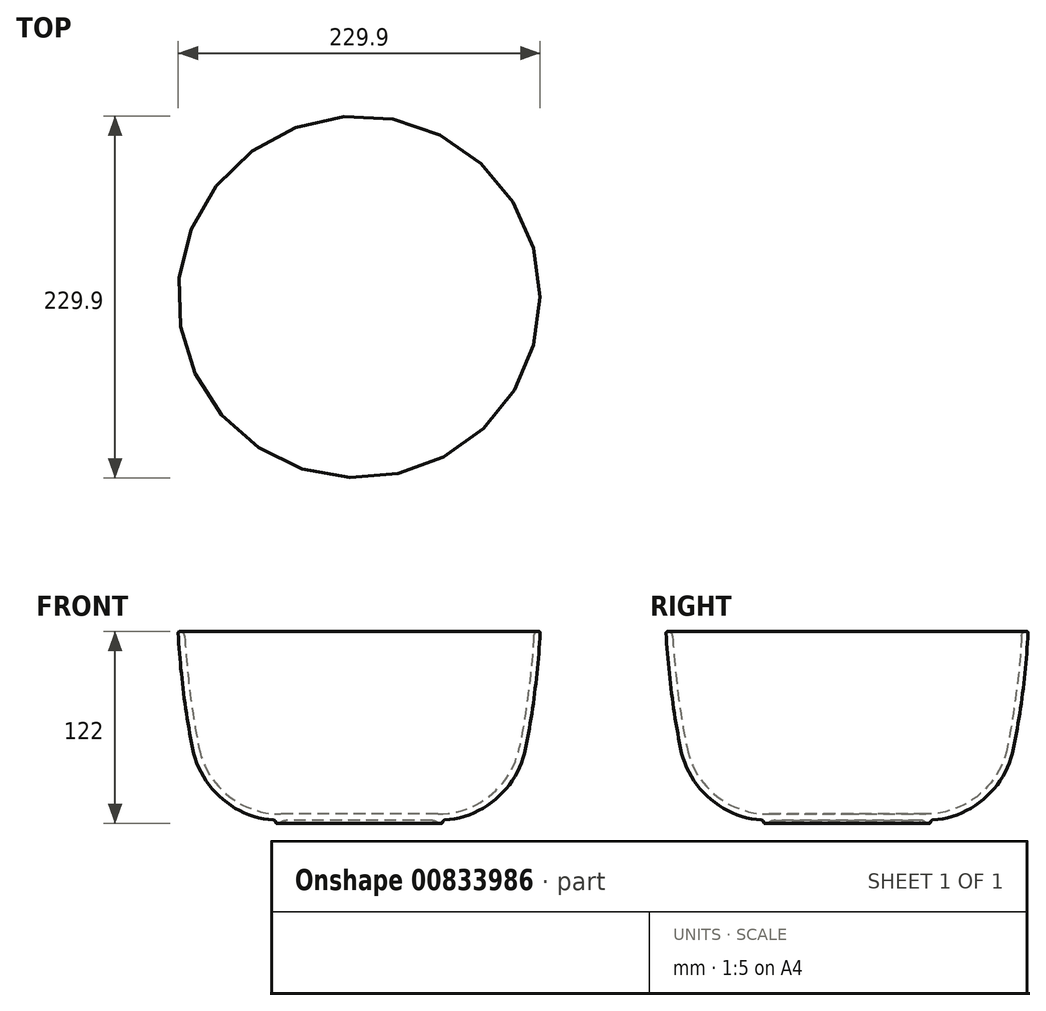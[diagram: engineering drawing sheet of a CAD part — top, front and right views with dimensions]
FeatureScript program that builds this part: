
annotation { "Feature Type Name" : "Feature", "Feature Type Description" : "" }
export const myFeature = defineFeature(function(context is Context, id is Id, definition is map)
    precondition{}
    {
        {
            var Q0;
            Q0=qCreatedBy(makeId("Front.planeOp"),FACE);
            var sketch = newSketch(context, id + "F0", { "sketchPlane" : qUnion([Q0])});
            skLineSegment(sketch, "E0", {"start": v(0, 0) * mm, "end": v(-50, 0) * mm});
            skArc(sketch, "E1", {"start": v(-105.76, 45.79) * mm, "mid": v(-97.1, 25.02) * mm, "end": v(-81.07, 9.24) * mm});
            skLineSegment(sketch, "E2.0", {"start": v(0, 4) * mm, "end": v(-50, 4) * mm});
            skArc(sketch, "E2.1", {"start": v(-101.84, 46.57) * mm, "mid": v(-92.46, 25.39) * mm, "end": v(-74.93, 10.25) * mm});
            skLineSegment(sketch, "E3", {"start": v(0, 4) * mm, "end": v(0, 0) * mm});
            skLineSegment(sketch, "E4", {"start": v(-111, 120) * mm, "end": v(-115, 120) * mm});
            skArc(sketch, "E5", {"start": v(-74.93, 10.25) * mm, "mid": v(-62.85, 5.59) * mm, "end": v(-50, 4) * mm});
            skArc(sketch, "E6", {"start": v(-81.07, 9.24) * mm, "mid": v(-66.2, 2.36) * mm, "end": v(-50, 0) * mm});
            skArc(sketch, "E7", {"start": v(-111, 120) * mm, "mid": v(-107.73, 83.12) * mm, "end": v(-101.84, 46.57) * mm});
            skArc(sketch, "E8", {"start": v(-115, 120) * mm, "mid": v(-111.71, 82.73) * mm, "end": v(-105.76, 45.79) * mm});
            skLineSegment(sketch, "E9", {"start": v(-111, 120) * mm, "end": v(-105, 5.67) * mm, "construction": true});
            skLineSegment(sketch, "E10", {"start": v(-50, 0) * mm, "end": v(-50, -2) * mm});
            skLineSegment(sketch, "E11", {"start": v(-50, -2) * mm, "end": v(-53, -2) * mm});
            skLineSegment(sketch, "E12", {"start": v(-53, -2) * mm, "end": v(-53, 0.08) * mm});
            skSolve(sketch);
        }
        {
            var Q0;
            Q0 = qSketchRegion(id + "F0", true);
            var Q1;
            Q1=sQuery(id+"F0.wireOp",EDGE,"E3");
            revolve(context, id + "F1", {"surfaceOperationType" : NewSurfaceOperationType.NEW, "entities" : qUnion([Q0]), "axis" : qUnion([Q1]), "revolveType" : RevolveType.FULL});
        }
        {
            var Q0;
            Q0=makeQuery(id+"F1.opRevolve","SWEPT_EDGE",EDGE,{"disambiguationData":[OSD([sQuery(id+"F0.wireOp",EDGE,"E11"),sQuery(id+"F0.wireOp",EDGE,"E12")])]});
            var Q1;
            Q1=makeQuery(id+"F1.opRevolve","SWEPT_EDGE",EDGE,{"disambiguationData":[OSD([sQuery(id+"F0.wireOp",EDGE,"E10"),sQuery(id+"F0.wireOp",EDGE,"E11")])]});
            var Q2;
            Q2=makeQuery(id+"F1.opRevolve","SWEPT_EDGE",EDGE,{"disambiguationData":[OSD([sQuery(id+"F0.wireOp",EDGE,"E4"),sQuery(id+"F0.wireOp",EDGE,"E8")])]});
            fillet(context, id + "F2", {"entities" : qUnion([Q0, Q1, Q2]), "radius" : 1 * mm, "tangentPropagation" : true, "allowEdgeOverflow" : false});
        }
        {
            var Q0;
            Q0=makeQuery(id+"F1.opRevolve","SWEPT_EDGE",EDGE,{"disambiguationData":[OSD([sQuery(id+"F0.wireOp",EDGE,"E6"),sQuery(id+"F0.wireOp",EDGE,"E12")])]});
            fillet(context, id + "F3", {"entities" : qUnion([Q0]), "radius" : 1.5 * mm, "tangentPropagation" : true, "allowEdgeOverflow" : false});
        }
        {
            var Q0;
            Q0=makeQuery(id+"F1.opRevolve","SWEPT_FACE",FACE,{"disambiguationData":[OSD([sQuery(id+"F0.wireOp",EDGE,"E0")])]});
            fillet(context, id + "F4", {"entities" : qUnion([Q0]), "radius" : 5 * mm, "tangentPropagation" : true, "allowEdgeOverflow" : false});
        }
        {
            var Q0;
            Q0=makeQuery(id+"F1.opRevolve","SWEPT_EDGE",EDGE,{"disambiguationData":[OSD([sQuery(id+"F0.wireOp",EDGE,"E4"),sQuery(id+"F0.wireOp",EDGE,"E7")])]});
            fillet(context, id + "F5", {"entities" : qUnion([Q0]), "radius" : 3 * mm, "tangentPropagation" : true, "allowEdgeOverflow" : false});
        }
    });
